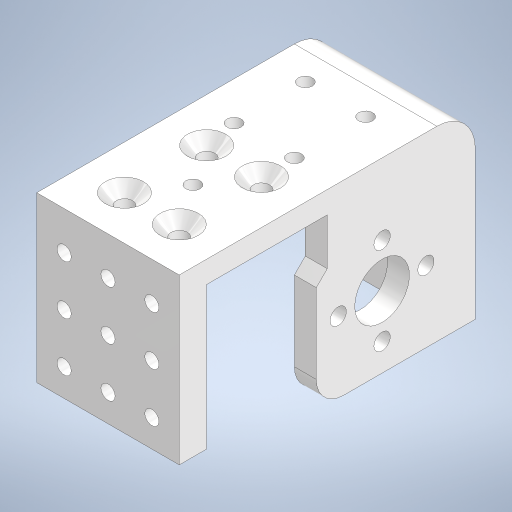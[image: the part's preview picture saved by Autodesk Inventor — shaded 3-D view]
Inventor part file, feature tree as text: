
AUTODESK INVENTOR PART (.ipt)
format: ipt  version: 2024.1 (Build 281209000, 209)  size: 450,560 bytes
history: native  units: mm
features: extrude x12, sketch x12, fillet x3, chamfer x2, mirror x1
ambient origin geometry x8: Origin, YZ Plane, XZ Plane, XY Plane, X Axis, Y Axis, Z Axis, Center Point
bodies: Solid1 (feature_tree)
feature tree (30):
  extrude  "Extrusion1"  Depth=26.0mm
  extrude  "Extrusion2"  Depth=4.0mm
  extrude  "Extrusion3"  Depth=30.0mm TaperAngle=0.0deg
  extrude  "Extrusion4"  Depth=10.0mm
  extrude  "Extrusion6"  TaperAngle=0.0deg  [1 undecoded]
  fillet  "Fillet3"  Radius=3.0mm
  fillet  "Fillet4"  Radius=3.0mm
  fillet  "Fillet5"  Radius=3.0mm
  extrude  "Extrusion7"  Depth=8.0mm
  extrude  "Extrusion8"  Depth=8.0mm
  extrude  "Extrusion9"  Depth=8.0mm
  chamfer  "Chamfer3"  [1 undecoded]
  extrude  "Extrusion10"  Depth=5.0mm
  extrude  "Extrusion11"  Depth=1.5mm
  mirror  "Mirror1"
  extrude  "Extrusion13"  Depth=30.0mm
  chamfer  "Chamfer4"  Distance=5.0mm
  extrude  "Extrusion14"  Depth=2.0mm
  sketch  "Sketch1"  dims[d0=45.0mm d1=26.0mm]
  sketch  "Sketch2"  dims[d2=4.0mm d3=0.0mm d4=4.0mm]
  sketch  "Sketch4"  dims[d5=25.0mm d6=30.0mm d7=0.0mm]
  sketch  "Sketch5"  dims[d8=10.0mm d9=13.0mm]
  sketch  "Sketch9"  dims[d10=13.0mm d11=0.0mm d12=0.0mm d13=3.0mm d14=3.0mm d15=3.0mm]
  sketch  "Sketch10"  dims[d16=3.0mm d17=8.0mm]
  sketch  "Sketch12"  dims[d19=8.0mm d20=8.0mm]
  sketch  "Sketch13"  dims[d21=8.0mm d22=8.0mm]
  sketch  "Sketch14"  dims[d23=8.0mm]
  sketch  "Sketch15"  dims[d24=8.0mm d25=0.0mm d26=0.0mm]
  sketch  "Sketch17"  dims[d39=4.0mm d40=0.0mm d41=5.0mm]
  sketch  "Sketch18"  dims[d42=7.0mm d43=1.5mm d44=30.0mm d45=5.0mm d46=0.0mm d47=2.6mm d48=2.6mm d49=2.6mm d50=2.6mm d51=2.6mm d52=5.0mm d53=5.0mm d54=5.0mm d55=5.0mm d56=7.0mm d57=7.0mm d58=16.0mm d59=5.0mm d60=5.0mm d61=5.0mm d62=10.0mm d63=0.0mm d64=2.6mm d65=16.0mm d66=5.0mm d67=3.0mm d68=3.0mm d69=3.0mm d70=3.0mm d71=10.0mm d72=15.0mm d73=15.0mm d74=8.0mm d75=8.0mm d76=8.0mm d77=8.0mm d78=10.0mm d79=0.0mm d80=0.0mm d81=2.6mm d82=2.6mm d83=2.6mm d84=5.0mm d85=13.0mm d86=13.0mm d87=13.0mm d88=7.0mm d89=16.0mm d90=2.0mm d91=2.0mm d92=45.0deg d93=2.6mm d94=2.6mm d95=2.6mm d96=2.6mm d97=8.0mm d98=8.0mm d99=6.0mm d100=6.0mm d101=8.0mm d102=8.0mm d103=10.0mm d104=10.0mm d105=0.0mm d106=0.0mm d107=2.6mm d108=2.6mm d109=2.6mm d110=2.6mm d111=8.0mm d112=8.0mm d113=7.0mm d114=7.0mm d115=13.0mm d116=13.0mm d117=29.0mm d118=29.0mm d119=10.0mm d120=0.0mm d124=2.0mm d125=8.5mm d126=0.0mm d127=0.0mm d128=2.0mm d129=2.0mm d130=45.0deg d131=2.6mm d132=15.5mm d133=13.0mm d134=0.0mm d135=0.0mm]
note: 2 required parameter values undecoded (feature->parameter linkage not recoverable at this tier; creation-order binding heuristic only, values carry confidence <= 0.55)
